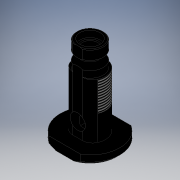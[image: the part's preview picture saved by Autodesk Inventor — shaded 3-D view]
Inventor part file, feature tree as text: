
AUTODESK INVENTOR PART (.ipt)
format: ipt  version: 2019 (Build 230136000, 136)  size: 220,672 bytes
history: native  units: mm
features: other x7, extrude x3, hole x2, chamfer x2
ambient origin geometry x8: Origin, YZ Plane, XZ Plane, XY Plane, X Axis, Y Axis, Z Axis, Center Point
bodies: Solid1 (feature_tree)
feature tree (14):
  extrude  "Spigot Base"  Depth=19.0mm
  extrude  "Spigot"  Depth=9.5mm
  other  "Spigot Axis"
  other  "Clip Cutout"
  hole  "Connector Hole"  [1 undecoded]
  extrude  "Orientation Cutout"  Depth=8.0mm
  hole  "Cable Hole"  [1 undecoded]
  chamfer  "Top Chamfer"  Distance=3.0mm
  chamfer  "Bottom Chamfer"  Distance=9.9mm
  other  "Spigot Base Outline"
  other  "Spigot Cross Section"
  other  "Clip Cutout Profile"
  other  "Orientation Cutout Profile"
  other  "Cable Hole Position"
note: 2 required parameter values undecoded (feature->parameter linkage not recoverable at this tier; creation-order binding heuristic only, values carry confidence <= 0.55)
